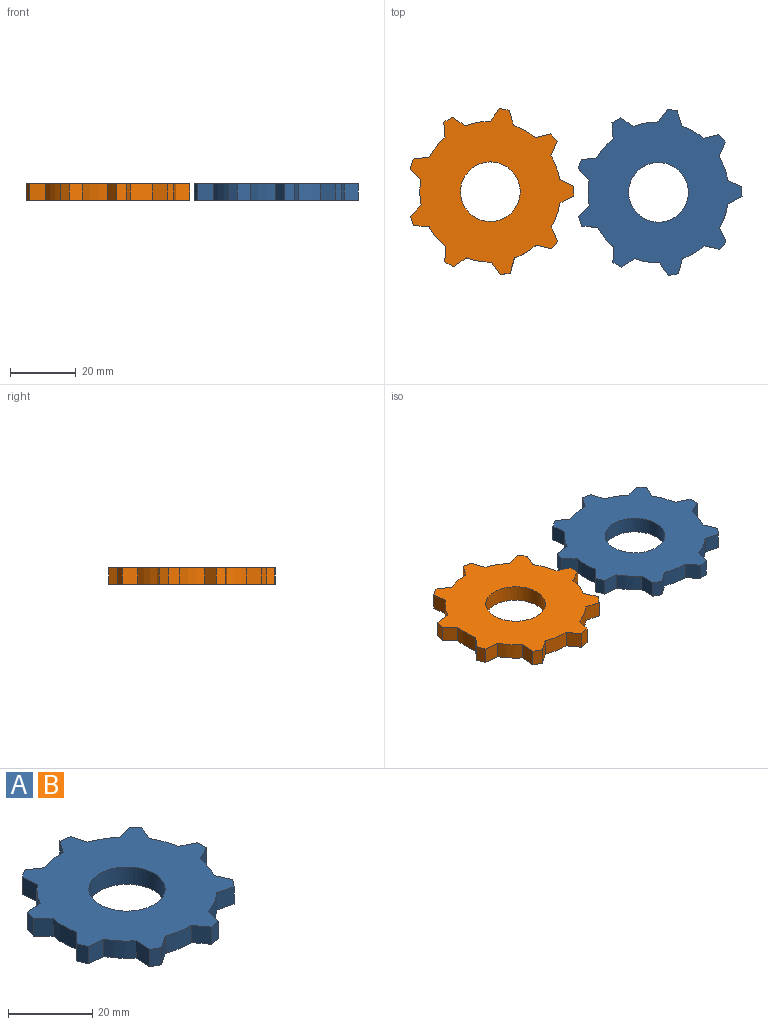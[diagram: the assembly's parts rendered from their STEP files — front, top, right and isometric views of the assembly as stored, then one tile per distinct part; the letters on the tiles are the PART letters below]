
ASSEMBLY  parts=2 mates=1
PART A: 39 faces, bbox 49.7x50.4x5 mm
  f0: plane 5x4.72mm, normal (-1,-0.08,0), area 23.7mm2, adj f1,f35,f37,f38
  f1: cylinder r=21.39mm len=5.93mm, axis (0,0,-1), area 38.7mm2, adj f0,f2,f37,f38
  f2: plane 5x4.71mm, normal (-0.11,0.99,0), area 23.7mm2, adj f1,f3,f37,f38
  f3: plane 5x2.83mm, normal (-0.94,0.34,0), area 15mm2, adj f2,f4,f37,f38
  f4: plane 5x3.39mm, normal (-0.71,-0.7,0), area 23.7mm2, adj f3,f5,f37,f38
  f5: cylinder r=21.39mm len=7.7mm, axis (0,0,-1), area 38.7mm2, adj f4,f6,f37,f38
  f6: plane 5x3.43mm, normal (-0.72,0.69,0), area 23.7mm2, adj f5,f7,f37,f38
  f7: plane 5x2.81mm, normal (-0.94,-0.35,0), area 15mm2, adj f6,f8,f37,f38
  f8: plane 5x4.71mm, normal (-0.1,-1,0), area 23.7mm2, adj f7,f9,f37,f38
  f9: cylinder r=21.39mm len=5.87mm, axis (0,0,-1), area 38.7mm2, adj f8,f10,f37,f38
  f10: plane 5x4.73mm, normal (-1,0.06,0), area 23.7mm2, adj f9,f11,f37,f38
  f11: plane 5x2.61mm, normal (-0.49,-0.87,0), area 15mm2, adj f10,f12,f37,f38
  f12: plane 5x3.91mm, normal (0.56,-0.83,0), area 23.7mm2, adj f11,f13,f37,f38
  f13: cylinder r=21.39mm len=7.6mm, axis (0,0,-1), area 38.7mm2, adj f12,f14,f37,f38
  f14: plane 5x3.81mm, normal (-0.81,-0.59,0), area 23.7mm2, adj f13,f15,f37,f38
  f15: plane 5x2.95mm, normal (0.18,-0.98,0), area 15mm2, adj f14,f16,f37,f38
  f16: plane 5x4.56mm, normal (0.96,-0.27,0), area 23.7mm2, adj f15,f17,f37,f38
  f17: cylinder r=21.39mm len=6.65mm, axis (0,0,-1), area 38.7mm2, adj f16,f18,f37,f38
  f18: plane 5x4.6mm, normal (-0.24,-0.97,0), area 23.7mm2, adj f17,f19,f37,f38
  f19: plane 5x2.31mm, normal (0.77,-0.64,0), area 15mm2, adj f18,f20,f37,f38
  f20: plane 5x4.31mm, normal (0.91,0.41,0), area 23.7mm2, adj f19,f21,f37,f38
  f21: cylinder r=21.39mm len=7.26mm, axis (0,0,-1), area 38.7mm2, adj f20,f22,f37,f38
  f22: plane 5x4.24mm, normal (0.44,-0.9,0), area 23.7mm2, adj f21,f23,f37,f38
  f23: plane 5x3mm, normal (1,0.01,0), area 15mm2, adj f22,f24,f37,f38
  f24: plane 5x4.27mm, normal (0.43,0.9,0), area 23.7mm2, adj f23,f25,f37,f38
  f25: cylinder r=21.39mm len=7.22mm, axis (0,0,-1), area 38.7mm2, adj f24,f26,f37,f38
  f26: plane 5x4.34mm, normal (0.92,-0.4,0), area 23.7mm2, adj f25,f27,f37,f38
  f27: plane 5x2.29mm, normal (0.76,0.65,0), area 15mm2, adj f26,f28,f37,f38
  f28: plane 5x4.59mm, normal (-0.25,0.97,0), area 23.7mm2, adj f27,f29,f37,f38
  f29: cylinder r=21.39mm len=6.7mm, axis (0,0,-1), area 38.7mm2, adj f28,f30,f37,f38
  f30: plane 5x4.54mm, normal (0.96,0.28,0), area 23.7mm2, adj f29,f31,f37,f38
  f31: plane 5x2.96mm, normal (0.17,0.99,0), area 15mm2, adj f30,f32,f37,f38
  f32: plane 5x3.85mm, normal (-0.81,0.58,0), area 23.7mm2, adj f31,f33,f37,f38
  f33: cylinder r=21.39mm len=7.58mm, axis (0,0,-1), area 38.7mm2, adj f32,f34,f37,f38
  f34: plane 5x3.94mm, normal (0.55,0.83,0), area 23.7mm2, adj f33,f35,f37,f38
  f35: plane 5x2.59mm, normal (-0.51,0.86,0), area 15mm2, adj f0,f34,f37,f38
  f36: cylinder r=9.05mm len=18.11mm, axis (0,0,-1), area 284.4mm2, adj f37,f38
  f37: plane 50.44x49.73mm, normal (0,0,1), area 1361.4mm2, adj f0,f1,f2,f3,f4,f5,f6,f7
  f38: plane 50.44x49.73mm, normal (0,0,-1), area 1361.4mm2, adj f0,f1,f2,f3,f4,f5,f6,f7
PART B: same geometry as A
PLACE A t=(34.69,-3.94,5.62)mm
PLACE B t=(-16.33,-3.75,5.62)mm
MATE slider A.f37 <-> B.f37  axis (0,0,1) through (13.67,6.25,10.62)mm
